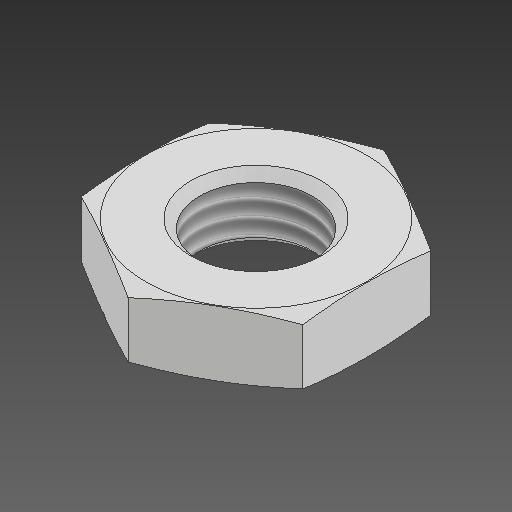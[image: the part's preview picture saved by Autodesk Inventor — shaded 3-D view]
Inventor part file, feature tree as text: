
AUTODESK INVENTOR PART (.ipt)
format: ipt  version: 2021 (Build 250183000, 183)  size: 158,720 bytes
history: native  units: in
note: dims shown in document units (in); Inventor stores cm internally (conversion verified against a paired STEP export)
features: other x18, sketch x3
ambient origin geometry x8: Origin, YZ Plane, XZ Plane, XY Plane, X Axis, Y Axis, Z Axis, Center Point
bodies: Solid1 (feature_tree)
feature tree (21):
  other  "DIN-439-B - M10x1_25(F).ipt"
  other  "Solid1::DIN-439-B - M10x1_25(F).ipt"
  other  "TaggingFeature1"
  sketch  "Sketch_1"  dims[d0=0.3937in]
  sketch  "Sketch_2"  dims[d6=0.0in]
  sketch  "Sketch_3"
  other  "2CYL_XY"
  other  "2CYL_YZ"
  other  "2CYL_ZX"
  other  "din439b_punkt_XY"
  other  "din439b_punkt_YZ"
  other  "din439b_punkt_ZX"
  other  "2CYL_X"
  other  "2CYL_Y"
  other  "2CYL_Z"
  other  "din439b_punkt_X"
  other  "din439b_punkt_Y"
  other  "din439b_punkt_Z"
  other  "2CYL_Center"
  other  "din439b_punkt_Center"
  other  "din439b_punkt"
